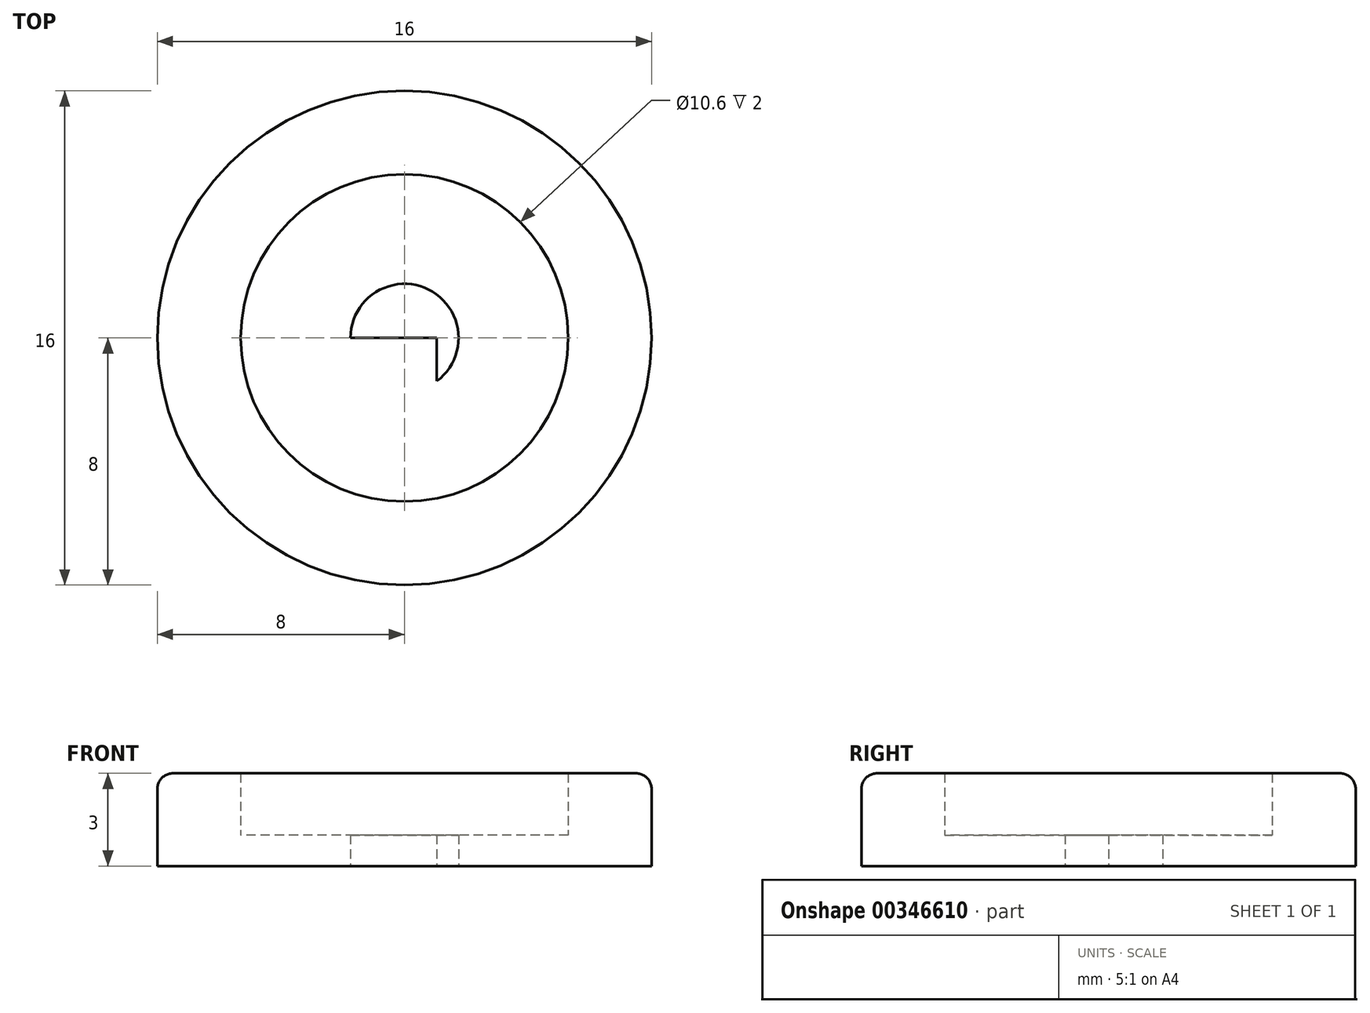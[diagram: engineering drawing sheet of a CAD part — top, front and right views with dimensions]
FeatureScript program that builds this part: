
annotation { "Feature Type Name" : "Feature", "Feature Type Description" : "" }
export const myFeature = defineFeature(function(context is Context, id is Id, definition is map)
    precondition{}
    {
        {
            var Q0;
            Q0=qCreatedBy(makeId("Top.planeOp"),FACE);
            var sketch = newSketch(context, id + "F0", { "sketchPlane" : qUnion([Q0])});
            skCircle(sketch, "E0", {"center": v(0, 0) * mm, "radius": 8 * mm});
            skCircle(sketch, "E1", {"center": v(0, 0) * mm, "radius": 5.3 * mm});
            skCircle(sketch, "E2", {"center": v(0, 0) * mm, "radius": 1.75 * mm});
            skLineSegment(sketch, "E3", {"start": v(-1.75, 0) * mm, "end": v(1.05, 0) * mm});
            skLineSegment(sketch, "E4", {"start": v(1.05, 0) * mm, "end": v(1.05, 1.4) * mm});
            skLineSegment(sketch, "E5", {"start": v(1.05, 1.4) * mm, "end": v(1.05, -1.4) * mm});
            skSolve(sketch);
        }
        {
            var Q0;
            {var subQ0=sQuery(id+"F0.wireOp",EDGE,"E5");var subQ1=sQuery(id+"F0.wireOp",EDGE,"E2");var subQ2=makeQuery(id+"F0.imprint","INTERSECT",VERTEX,{"disambiguationData":[OD(0.0)],"derivedFrom":[subQ1,subQ0]});Q0=makeQuery(id+"F0.imprint","IMPRINT",FACE,{"disambiguationData":[TD([[makeQuery(id+"F0.imprint","IMPRINT",EDGE,{"disambiguationData":[TD([[subQ2,1.0]])],"derivedFrom":subQ1}),1.0]])]});}
            var Q1;
            Q1=makeQuery(id+"F0.imprint","IMPRINT",FACE,{"disambiguationData":[TD([[makeQuery(id+"F0.imprint","IMPRINT",EDGE,{"derivedFrom":sQuery(id+"F0.wireOp",EDGE,"E1")}),1.0]])]});
            extrude(context, id + "F1", {"entities" : qUnion([Q0, Q1]), "depth" : 1 * mm});
        }
        {
            var Q0;
            Q0=makeQuery(id+"F0.imprint","IMPRINT",FACE,{"disambiguationData":[TD([[makeQuery(id+"F0.imprint","IMPRINT",EDGE,{"derivedFrom":sQuery(id+"F0.wireOp",EDGE,"E0")}),1.0]])]});
            extrude(context, id + "F2", {"entities" : qUnion([Q0]), "operationType" : NewBodyOperationType.ADD, "depth" : 3 * mm});
        }
        {
            var Q0;
            Q0=makeQuery(id+"F2.opExtrude","CAP_EDGE",EDGE,{"disambiguationData":[OSD([sQuery(id+"F0.wireOp",EDGE,"E0")])],"isStart":false});
            fillet(context, id + "F3", {"entities" : qUnion([Q0]), "radius" : 0.5 * mm, "tangentPropagation" : true, "allowEdgeOverflow" : false});
        }
    });
